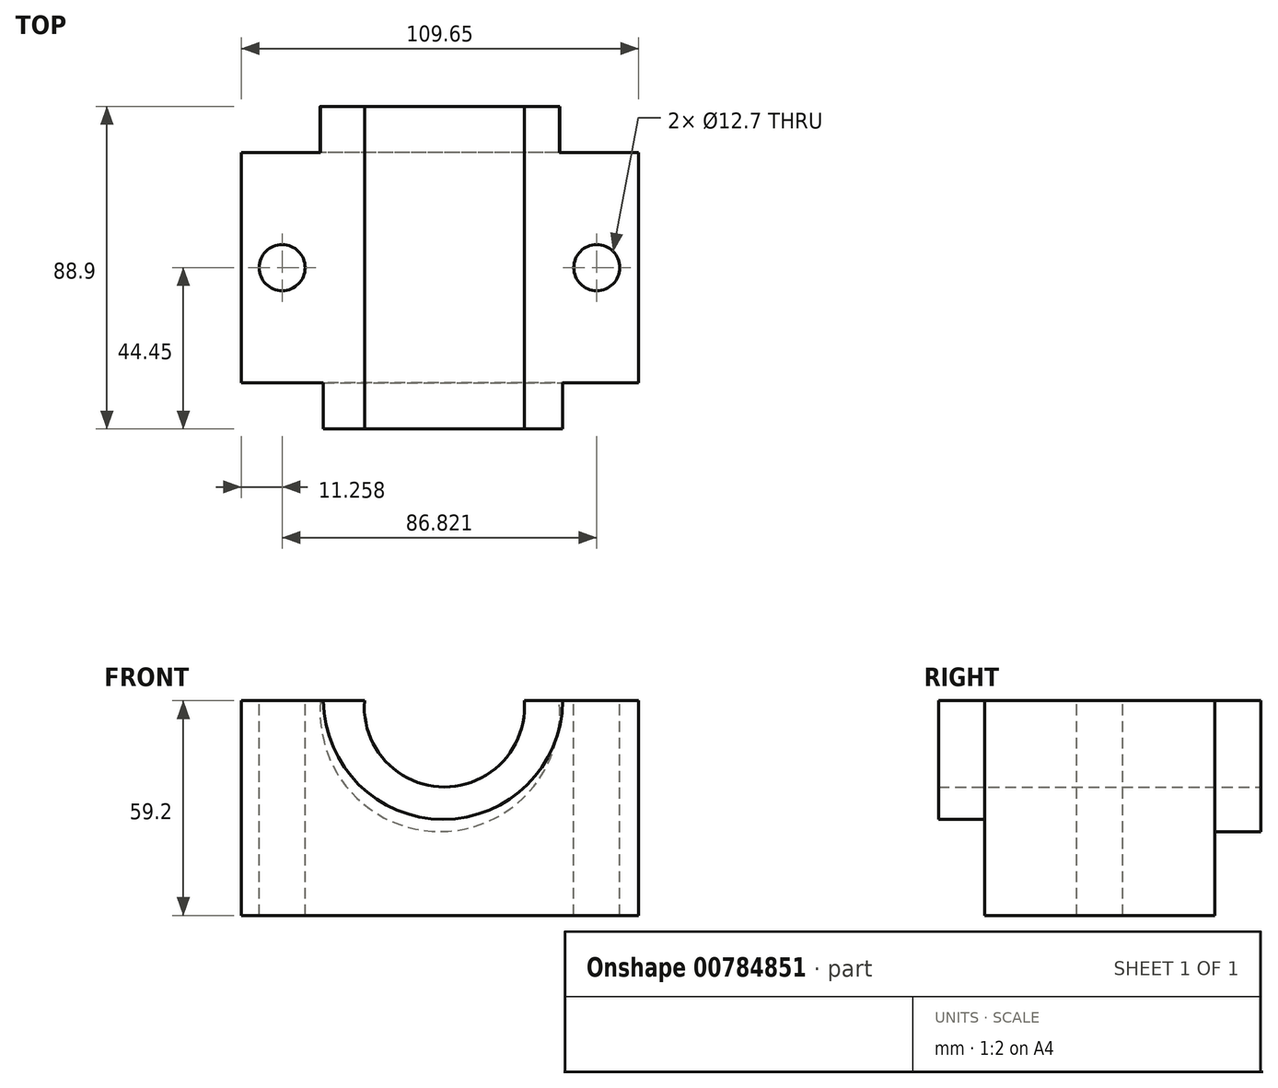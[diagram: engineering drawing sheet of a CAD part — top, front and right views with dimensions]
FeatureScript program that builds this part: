
annotation { "Feature Type Name" : "Feature", "Feature Type Description" : "" }
export const myFeature = defineFeature(function(context is Context, id is Id, definition is map)
    precondition{}
    {
        {
            var Q0;
            Q0=qCreatedBy(makeId("Front.planeOp"),FACE);
            var sketch = newSketch(context, id + "F0", { "sketchPlane" : qUnion([Q0])});
            skLineSegment(sketch, "E0", {"start": v(-42.75, 37.15) * mm, "end": v(-29.95, 37.15) * mm});
            skLineSegment(sketch, "E1", {"start": v(28.44, 37.15) * mm, "end": v(41.24, 37.15) * mm});
            skLineSegment(sketch, "E2", {"start": v(-29.95, 37.15) * mm, "end": v(-23.01, 37.15) * mm});
            skLineSegment(sketch, "E3", {"start": v(20.36, 37.15) * mm, "end": v(28.44, 37.15) * mm});
            skLineSegment(sketch, "E4", {"start": v(-42.75, 37.15) * mm, "end": v(-55.55, 37.15) * mm});
            skLineSegment(sketch, "E5", {"start": v(-55.55, 37.15) * mm, "end": v(-55.55, -22.05) * mm});
            skLineSegment(sketch, "E6", {"start": v(41.24, 37.15) * mm, "end": v(54.1, 37.15) * mm});
            skLineSegment(sketch, "E7", {"start": v(54.1, 37.15) * mm, "end": v(54.1, -22.05) * mm});
            skLineSegment(sketch, "E8", {"start": v(54.1, -22.05) * mm, "end": v(-55.55, -22.05) * mm});
            skLineSegment(sketch, "E9", {"start": v(-23.01, 37.15) * mm, "end": v(20.36, 37.15) * mm});
            skSolve(sketch);
        }
        {
            var Q0;
            Q0=makeQuery(id+"F0.imprint","IMPRINT",FACE,{"disambiguationData":[TD([[makeQuery(id+"F0.imprint","IMPRINT",EDGE,{"derivedFrom":sQuery(id+"F0.wireOp",EDGE,"E0")}),-1.0]])]});
            extrude(context, id + "F1", {"entities" : qUnion([Q0]), "oppositeDirection" : true, "depth" : 63.5 * mm, "offsetDistance" : 25.4 * mm});
        }
        {
            var Q0;
            Q0=makeQuery(id+"F1.opExtrude","CAP_FACE",FACE,{"disambiguationData":[OSD([sQuery(id+"F0.wireOp",EDGE,"E0"),sQuery(id+"F0.wireOp",EDGE,"E1"),sQuery(id+"F0.wireOp",EDGE,"E2"),sQuery(id+"F0.wireOp",EDGE,"E3"),sQuery(id+"F0.wireOp",EDGE,"E4"),sQuery(id+"F0.wireOp",EDGE,"E5"),sQuery(id+"F0.wireOp",EDGE,"E6"),sQuery(id+"F0.wireOp",EDGE,"E7"),sQuery(id+"F0.wireOp",EDGE,"E8"),sQuery(id+"F0.wireOp",EDGE,"E9")])],"isStart":true});
            var sketch = newSketch(context, id + "F2", { "sketchPlane" : qUnion([Q0])});
            skArc(sketch, "E10", {"start": v(-32.9, 37.15) * mm, "mid": v(0.12, 4.46) * mm, "end": v(33.14, 37.15) * mm});
            skArc(sketch, "E11", {"start": v(-21.57, 37.15) * mm, "mid": v(0.48, 13.37) * mm, "end": v(22.53, 37.15) * mm});
            skSolve(sketch);
        }
        {
            var Q0;
            {var subQ0=sQuery(id+"F2.wireOp",EDGE,"E10");Q0=makeQuery(id+"F2.imprint","IMPRINT",FACE,{"disambiguationData":[TD([[makeQuery(id+"F2.imprint","IMPRINT",EDGE,{"derivedFrom":subQ0}),1.0]])]});}
            extrude(context, id + "F3", {"entities" : qUnion([Q0]), "operationType" : NewBodyOperationType.ADD, "depth" : 12.7 * mm, "offsetDistance" : 25.4 * mm});
        }
        {
            var Q0;
            {var subQ0=sQuery(id+"F0.wireOp",EDGE,"E9");var subQ1=sQuery(id+"F0.wireOp",EDGE,"E6");var subQ2=sQuery(id+"F0.wireOp",EDGE,"E4");var subQ3=sQuery(id+"F0.wireOp",EDGE,"E3");var subQ4=sQuery(id+"F0.wireOp",EDGE,"E2");var subQ5=sQuery(id+"F0.wireOp",EDGE,"E1");var subQ6=sQuery(id+"F0.wireOp",EDGE,"E0");var subQ9=sQuery(id+"F2.wireOp",EDGE,"E11");Q0=makeQuery(id+"F3.boolean.opBoolean","SPLIT",FACE,{"disambiguationData":[TD([makeQuery(id+"F3.opExtrude","SWEPT_FACE",FACE,{"disambiguationData":[OSD([subQ9])]})])],"derivedFrom":makeQuery(id+"F1.opExtrude","CAP_FACE",FACE,{"disambiguationData":[OSD([subQ6,subQ5,subQ4,subQ3,subQ2,sQuery(id+"F0.wireOp",EDGE,"E5"),subQ1,sQuery(id+"F0.wireOp",EDGE,"E7"),sQuery(id+"F0.wireOp",EDGE,"E8"),subQ0])],"isStart":true})});}
            extrude(context, id + "F4", {"entities" : qUnion([Q0]), "operationType" : NewBodyOperationType.REMOVE, "endBound" : BoundingType.THROUGH_ALL, "oppositeDirection" : true, "depth" : 25.4 * mm, "offsetDistance" : 25.4 * mm});
        }
        {
            var Q0;
            Q0=makeQuery(id+"F1.opExtrude","CAP_FACE",FACE,{"disambiguationData":[OSD([sQuery(id+"F0.wireOp",EDGE,"E0"),sQuery(id+"F0.wireOp",EDGE,"E1"),sQuery(id+"F0.wireOp",EDGE,"E2"),sQuery(id+"F0.wireOp",EDGE,"E3"),sQuery(id+"F0.wireOp",EDGE,"E4"),sQuery(id+"F0.wireOp",EDGE,"E5"),sQuery(id+"F0.wireOp",EDGE,"E6"),sQuery(id+"F0.wireOp",EDGE,"E7"),sQuery(id+"F0.wireOp",EDGE,"E8"),sQuery(id+"F0.wireOp",EDGE,"E9")])],"isStart":false});
            var sketch = newSketch(context, id + "F5", { "sketchPlane" : qUnion([Q0])});
            skArc(sketch, "E12", {"start": v(-32.17, 37.15) * mm, "mid": v(0.76, 1.07) * mm, "end": v(33.69, 37.15) * mm});
            skSolve(sketch);
        }
        {
            var Q0;
            {var subQ0=sQuery(id+"F5.wireOp",EDGE,"E12");Q0=makeQuery(id+"F5.imprint","IMPRINT",FACE,{"disambiguationData":[TD([[makeQuery(id+"F5.imprint","IMPRINT",EDGE,{"derivedFrom":subQ0}),1.0]])]});}
            extrude(context, id + "F6", {"entities" : qUnion([Q0]), "operationType" : NewBodyOperationType.ADD, "depth" : 12.7 * mm, "offsetDistance" : 25.4 * mm});
        }
        {
            var Q0;
            {var subQ0=sQuery(id+"F0.wireOp",EDGE,"E5");var subQ1=makeQuery(id+"F1.opExtrude","SWEPT_FACE",FACE,{"disambiguationData":[OSD([subQ0])]});var subQ2=sQuery(id+"F0.wireOp",EDGE,"E9");var subQ3=sQuery(id+"F0.wireOp",EDGE,"E6");var subQ4=sQuery(id+"F0.wireOp",EDGE,"E4");var subQ5=sQuery(id+"F0.wireOp",EDGE,"E3");var subQ6=sQuery(id+"F0.wireOp",EDGE,"E2");var subQ7=sQuery(id+"F0.wireOp",EDGE,"E1");var subQ8=sQuery(id+"F0.wireOp",EDGE,"E0");var subQ9=makeQuery(id+"F1.opExtrude","SWEPT_FACE",FACE,{"disambiguationData":[OSD([subQ8,subQ7,subQ6,subQ5,subQ4,subQ3,subQ2])]});var subQ15=sQuery(id+"F2.wireOp",EDGE,"E10");var subQ16=makeQuery(id+"F1.opExtrude","CAP_EDGE",EDGE,{"disambiguationData":[OSD([subQ8,subQ7,subQ6,subQ5,subQ4,subQ3,subQ2])],"isStart":true});var subQ17=makeQuery(id+"F3.opExtrude","SWEPT_FACE",FACE,{"disambiguationData":[OSD([subQ8,subQ7,subQ6,subQ5,subQ4,subQ3,subQ2]),TDD([makeQuery(id+"F2.imprint","IMPRINT",EDGE,{"disambiguationData":[TD([[makeQuery(id+"F2.imprint","INTERSECT",VERTEX,{"disambiguationData":[OD(0.0)],"derivedFrom":[subQ16,subQ15]}),-1.0]])],"derivedFrom":subQ16})])]});var subQ18=makeQuery(id+"F3.opExtrude","SWEPT_FACE",FACE,{"disambiguationData":[OSD([subQ8,subQ7,subQ6,subQ5,subQ4,subQ3,subQ2]),TDD([makeQuery(id+"F2.imprint","IMPRINT",EDGE,{"disambiguationData":[TD([[makeQuery(id+"F2.imprint","INTERSECT",VERTEX,{"disambiguationData":[OD(1.0)],"derivedFrom":[subQ16,subQ15]}),1.0]])],"derivedFrom":subQ16})])]});var subQ20=makeQuery(id+"F4.boolean.opBoolean","SPLIT",EDGE,{"disambiguationData":[TD([subQ1])],"derivedFrom":makeQuery(id+"F1.opExtrude","CAP_EDGE",EDGE,{"disambiguationData":[OSD([subQ8,subQ7,subQ6,subQ5,subQ4,subQ3,subQ2])],"isStart":false})});Q0=makeQuery(id+"F6.boolean.opBoolean","MERGE",FACE,{"derivedFrom":[makeQuery(id+"F4.boolean.opBoolean","SPLIT",FACE,{"disambiguationData":[TD([subQ1])],"derivedFrom":makeQuery(id+"F3.boolean.opBoolean","MERGE",FACE,{"derivedFrom":[subQ9,subQ17,subQ18]})}),makeQuery(id+"F6.opExtrude","SWEPT_FACE",FACE,{"disambiguationData":[OSD([subQ8,subQ7,subQ6,subQ5,subQ4,subQ3,subQ2]),TDD([makeQuery(id+"F5.imprint","IMPRINT",EDGE,{"disambiguationData":[TD([[makeQuery(id+"F5.imprint","INTERSECT",VERTEX,{"derivedFrom":[subQ20,sQuery(id+"F5.wireOp",EDGE,"E12")]}),-1.0]])],"derivedFrom":subQ20})])]})]});}
            var sketch = newSketch(context, id + "F7", { "sketchPlane" : qUnion([Q0])});
            skPoint(sketch, "E13.centerSnap0", {"position": v(-55.55, 31.75) * mm});
            skCircle(sketch, "E14", {"center": v(-44.3, 31.75) * mm, "radius": 4.83 * mm});
            skCircle(sketch, "E15", {"center": v(42.53, 31.75) * mm, "radius": 4.83 * mm});
            skPoint(sketch, "E15.centerSnap0", {"position": v(-21.57, 31.75) * mm});
            skSolve(sketch);
        }
        {
            var Q0;
            Q0=sQuery(id+"F7.wireOp",VERTEX,"E14.center");
            var Q1;
            Q1=sQuery(id+"F7.wireOp",VERTEX,"E15.center");
            var Q2;
            Q2=makeQuery(id+"F1.opExtrude","SWEPT_BODY",BODY,{"disambiguationData":[OSD([sQuery(id+"F0.wireOp",EDGE,"E0"),sQuery(id+"F0.wireOp",EDGE,"E1"),sQuery(id+"F0.wireOp",EDGE,"E2"),sQuery(id+"F0.wireOp",EDGE,"E3"),sQuery(id+"F0.wireOp",EDGE,"E4"),sQuery(id+"F0.wireOp",EDGE,"E5"),sQuery(id+"F0.wireOp",EDGE,"E6"),sQuery(id+"F0.wireOp",EDGE,"E7"),sQuery(id+"F0.wireOp",EDGE,"E8"),sQuery(id+"F0.wireOp",EDGE,"E9")])]});
            hole(context, id + "F8", {"style" : HoleStyle.SIMPLE, "endStyle" : HoleEndStyle.BLIND, "holeDiameter" : 12.7 * mm, "majorDiameter" : 6.35 * mm, "holeDepth" : 152.4 * mm, "isTappedThrough" : true, "tappedDepth" : 12.7 * mm, "tapClearance" : 3, "locations" : qUnion([Q0, Q1]), "scope" : qUnion([Q2])});
        }
    });
